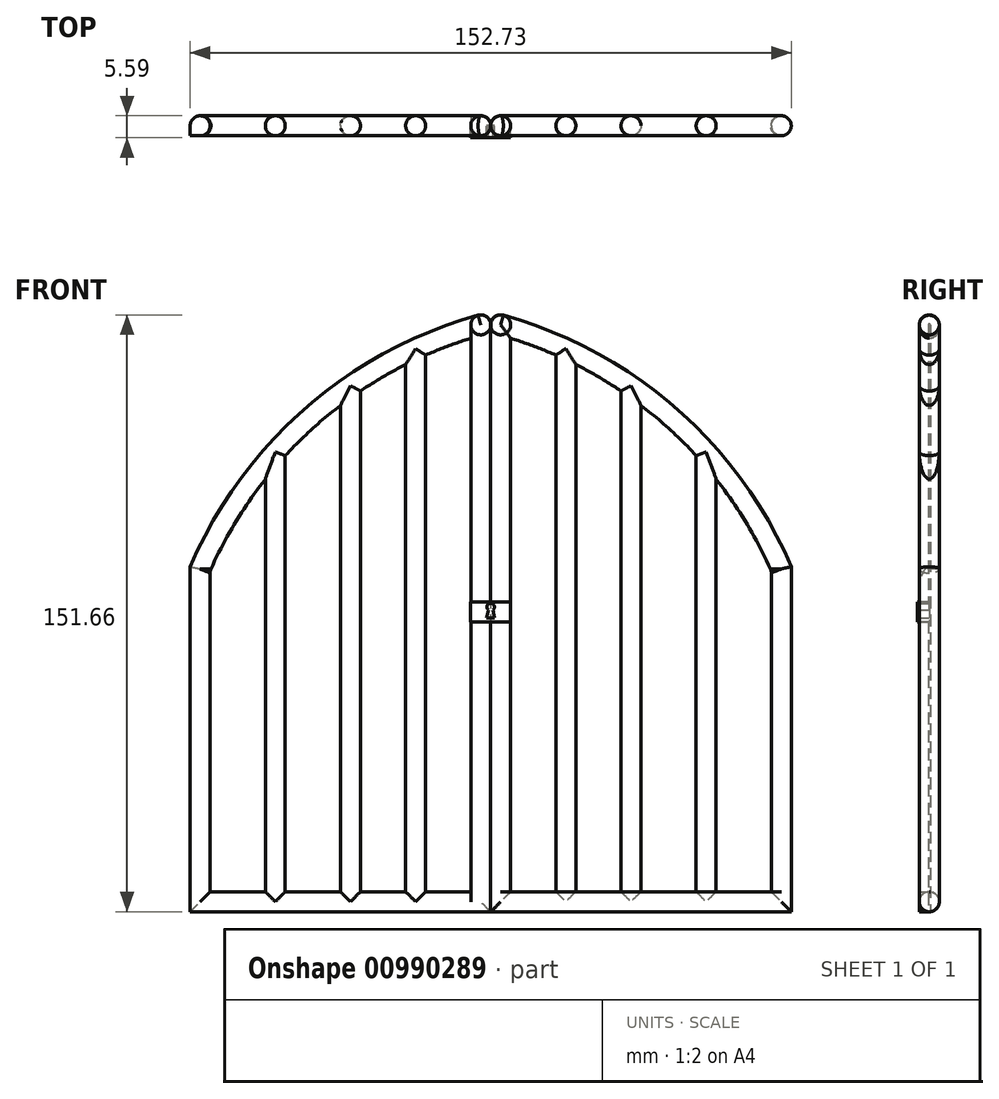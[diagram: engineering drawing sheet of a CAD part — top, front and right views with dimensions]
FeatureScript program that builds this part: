
annotation { "Feature Type Name" : "Feature", "Feature Type Description" : "" }
export const myFeature = defineFeature(function(context is Context, id is Id, definition is map)
    precondition{}
    {
        {
            var Q0;
            Q0=qCreatedBy(makeId("Front.planeOp"),FACE);
            var sketch = newSketch(context, id + "F0", { "sketchPlane" : qUnion([Q0])});
            skLineSegment(sketch, "E0", {"start": v(0, -76.2) * mm, "end": v(-76.38, -76.2) * mm});
            skLineSegment(sketch, "E1", {"start": v(-76.38, -76.2) * mm, "end": v(-76.38, 11.44) * mm});
            skArc(sketch, "E2", {"start": v(0, 76.2) * mm, "mid": v(-45.83, 52.84) * mm, "end": v(-76.38, 11.44) * mm});
            skLineSegment(sketch, "E3.MirrorCS", {"start": v(76.38, -76.2) * mm, "end": v(76.38, 11.44) * mm});
            skLineSegment(sketch, "E4.MirrorCS", {"start": v(0, -76.2) * mm, "end": v(76.38, -76.2) * mm});
            skArc(sketch, "E5.MirrorCS", {"start": v(0, 76.2) * mm, "mid": v(45.83, 52.84) * mm, "end": v(76.38, 11.44) * mm});
            skArc(sketch, "E6.0", {"start": v(5.08, 69.52) * mm, "mid": v(10.88, 67.54) * mm, "end": v(16.55, 65.23) * mm});
            skLineSegment(sketch, "E6.1", {"start": v(-71.3, -71.12) * mm, "end": v(-71.3, 10.4) * mm});
            skLineSegment(sketch, "E6.2", {"start": v(-5.08, -71.12) * mm, "end": v(-16.55, -71.12) * mm});
            skArc(sketch, "E6.3", {"start": v(-5.08, 69.52) * mm, "mid": v(-10.88, 67.54) * mm, "end": v(-16.55, 65.23) * mm});
            skLineSegment(sketch, "E6.4", {"start": v(5.08, -71.12) * mm, "end": v(16.55, -71.12) * mm});
            skLineSegment(sketch, "E6.5", {"start": v(71.3, -71.12) * mm, "end": v(71.3, 10.4) * mm});
            skLineSegment(sketch, "E7", {"start": v(-5.08, 69.52) * mm, "end": v(-5.08, -71.12) * mm});
            skLineSegment(sketch, "E8", {"start": v(5.08, 69.52) * mm, "end": v(5.08, -71.12) * mm});
            skLineSegment(sketch, "E9", {"start": v(33.1, -71.12) * mm, "end": v(33.1, 56.1) * mm});
            skLineSegment(sketch, "E10", {"start": v(38.19, -71.12) * mm, "end": v(38.19, 52.47) * mm});
            skLineSegment(sketch, "E11", {"start": v(16.55, -71.12) * mm, "end": v(16.55, 65.23) * mm});
            skLineSegment(sketch, "E12", {"start": v(21.63, -71.12) * mm, "end": v(21.63, 62.83) * mm});
            skLineSegment(sketch, "E13", {"start": v(38.19, -71.12) * mm, "end": v(52.2, -71.12) * mm});
            skLineSegment(sketch, "E14", {"start": v(52.2, -71.12) * mm, "end": v(52.2, 39.68) * mm});
            skLineSegment(sketch, "E15", {"start": v(57.28, -71.12) * mm, "end": v(57.28, 33.71) * mm});
            skLineSegment(sketch, "E16.MirrorCS", {"start": v(-16.55, -71.12) * mm, "end": v(-16.55, 65.23) * mm});
            skLineSegment(sketch, "E17.MirrorCS", {"start": v(-21.63, -71.12) * mm, "end": v(-21.63, 62.83) * mm});
            skLineSegment(sketch, "E18.MirrorCS", {"start": v(-33.1, -71.12) * mm, "end": v(-33.1, 56.1) * mm});
            skLineSegment(sketch, "E19.MirrorCS", {"start": v(-38.19, -71.12) * mm, "end": v(-38.19, 52.47) * mm});
            skLineSegment(sketch, "E20.MirrorCS", {"start": v(-52.2, -71.12) * mm, "end": v(-52.2, 39.68) * mm});
            skLineSegment(sketch, "E21.MirrorCS", {"start": v(-57.28, -71.12) * mm, "end": v(-57.28, 33.71) * mm});
            skPoint(sketch, "E22.end.orphan", {"position": v(-5.08, 70.96) * mm});
            skPoint(sketch, "E22.start.orphan", {"position": v(5.08, 70.96) * mm});
            skArc(sketch, "E23.trimOffspring", {"start": v(21.63, 62.83) * mm, "mid": v(27.48, 59.65) * mm, "end": v(33.1, 56.1) * mm});
            skArc(sketch, "E24.trimOffspring", {"start": v(38.19, 52.47) * mm, "mid": v(45.48, 46.38) * mm, "end": v(52.2, 39.68) * mm});
            skArc(sketch, "E25.trimOffspring", {"start": v(57.28, 33.71) * mm, "mid": v(65.03, 22.5) * mm, "end": v(71.3, 10.4) * mm});
            skLineSegment(sketch, "E26.trimOffspring", {"start": v(57.28, -71.12) * mm, "end": v(71.3, -71.12) * mm});
            skPoint(sketch, "E27.start.orphan", {"position": v(54.74, -71.12) * mm});
            skPoint(sketch, "E28.start.orphan", {"position": v(35.65, -71.12) * mm});
            skLineSegment(sketch, "E29.trimOffspring", {"start": v(21.63, -71.12) * mm, "end": v(33.1, -71.12) * mm});
            skPoint(sketch, "E30.start.orphan", {"position": v(19.1, -71.12) * mm});
            skPoint(sketch, "E31.orphan", {"position": v(0, -71.12) * mm});
            skLineSegment(sketch, "E32.trimOffspring", {"start": v(-21.63, -71.12) * mm, "end": v(-33.1, -71.12) * mm});
            skLineSegment(sketch, "E33.trimOffspring", {"start": v(-38.19, -71.12) * mm, "end": v(-52.2, -71.12) * mm});
            skLineSegment(sketch, "E34.trimOffspring", {"start": v(-57.28, -71.12) * mm, "end": v(-71.3, -71.12) * mm});
            skArc(sketch, "E35.trimOffspring", {"start": v(-57.28, 33.71) * mm, "mid": v(-65.03, 22.5) * mm, "end": v(-71.3, 10.4) * mm});
            skArc(sketch, "E36.trimOffspring", {"start": v(-21.63, 62.83) * mm, "mid": v(-27.48, 59.65) * mm, "end": v(-33.1, 56.1) * mm});
            skArc(sketch, "E37.trimOffspring", {"start": v(-38.19, 52.47) * mm, "mid": v(-45.48, 46.38) * mm, "end": v(-52.2, 39.68) * mm});
            skLineSegment(sketch, "E38", {"start": v(0, -76.2) * mm, "end": v(0, 76.2) * mm});
            skSolve(sketch);
        }
        {
            var Q0;
            Q0=makeQuery(id+"F0.imprint","IMPRINT",FACE,{"disambiguationData":[TD([[makeQuery(id+"F0.imprint","IMPRINT",EDGE,{"derivedFrom":sQuery(id+"F0.wireOp",EDGE,"E3.MirrorCS")}),1.0]])]});
            extrude(context, id + "F1", {"entities" : qUnion([Q0]), "depth" : 5.08 * mm, "offsetDistance" : 25.4 * mm});
        }
        {
            var Q0;
            Q0=makeQuery(id+"F0.imprint","IMPRINT",FACE,{"disambiguationData":[TD([[makeQuery(id+"F0.imprint","IMPRINT",EDGE,{"derivedFrom":sQuery(id+"F0.wireOp",EDGE,"E0")}),-1.0]])]});
            extrude(context, id + "F2", {"entities" : qUnion([Q0]), "depth" : 5.08 * mm, "offsetDistance" : 25.4 * mm});
        }
        {
            var Q0;
            Q0=makeQuery(id+"F1.opExtrude","CAP_EDGE",EDGE,{"disambiguationData":[OSD([sQuery(id+"F0.wireOp",EDGE,"E7")])],"isStart":false});
            var Q1;
            Q1=makeQuery(id+"F1.opExtrude","CAP_EDGE",EDGE,{"disambiguationData":[OSD([sQuery(id+"F0.wireOp",EDGE,"E8")])],"isStart":false});
            var Q2;
            Q2=makeQuery(id+"F1.opExtrude","CAP_EDGE",EDGE,{"disambiguationData":[OSD([sQuery(id+"F0.wireOp",EDGE,"E11")])],"isStart":false});
            var Q3;
            Q3=makeQuery(id+"F1.opExtrude","CAP_EDGE",EDGE,{"disambiguationData":[OSD([sQuery(id+"F0.wireOp",EDGE,"E12")])],"isStart":false});
            var Q4;
            Q4=makeQuery(id+"F1.opExtrude","CAP_EDGE",EDGE,{"disambiguationData":[OSD([sQuery(id+"F0.wireOp",EDGE,"E9")])],"isStart":false});
            var Q5;
            Q5=makeQuery(id+"F1.opExtrude","CAP_EDGE",EDGE,{"disambiguationData":[OSD([sQuery(id+"F0.wireOp",EDGE,"E10")])],"isStart":false});
            var Q6;
            Q6=makeQuery(id+"F1.opExtrude","CAP_EDGE",EDGE,{"disambiguationData":[OSD([sQuery(id+"F0.wireOp",EDGE,"E14")])],"isStart":false});
            var Q7;
            Q7=makeQuery(id+"F1.opExtrude","CAP_EDGE",EDGE,{"disambiguationData":[OSD([sQuery(id+"F0.wireOp",EDGE,"E15")])],"isStart":false});
            var Q8;
            Q8=makeQuery(id+"F1.opExtrude","CAP_EDGE",EDGE,{"disambiguationData":[OSD([sQuery(id+"F0.wireOp",EDGE,"E16.MirrorCS")])],"isStart":false});
            var Q9;
            Q9=makeQuery(id+"F1.opExtrude","CAP_EDGE",EDGE,{"disambiguationData":[OSD([sQuery(id+"F0.wireOp",EDGE,"E17.MirrorCS")])],"isStart":false});
            var Q10;
            Q10=makeQuery(id+"F1.opExtrude","CAP_EDGE",EDGE,{"disambiguationData":[OSD([sQuery(id+"F0.wireOp",EDGE,"E18.MirrorCS")])],"isStart":false});
            var Q11;
            Q11=makeQuery(id+"F1.opExtrude","CAP_EDGE",EDGE,{"disambiguationData":[OSD([sQuery(id+"F0.wireOp",EDGE,"E19.MirrorCS")])],"isStart":false});
            var Q12;
            Q12=makeQuery(id+"F1.opExtrude","CAP_EDGE",EDGE,{"disambiguationData":[OSD([sQuery(id+"F0.wireOp",EDGE,"E20.MirrorCS")])],"isStart":false});
            var Q13;
            Q13=makeQuery(id+"F1.opExtrude","CAP_EDGE",EDGE,{"disambiguationData":[OSD([sQuery(id+"F0.wireOp",EDGE,"E21.MirrorCS")])],"isStart":false});
            var Q14;
            Q14=makeQuery(id+"F1.opExtrude","CAP_EDGE",EDGE,{"disambiguationData":[OSD([sQuery(id+"F0.wireOp",EDGE,"E6.1")])],"isStart":false});
            var Q15;
            Q15=makeQuery(id+"F1.opExtrude","CAP_EDGE",EDGE,{"disambiguationData":[OSD([sQuery(id+"F0.wireOp",EDGE,"E1")])],"isStart":false});
            var Q16;
            Q16=makeQuery(id+"F1.opExtrude","CAP_EDGE",EDGE,{"disambiguationData":[OSD([sQuery(id+"F0.wireOp",EDGE,"E2")])],"isStart":false});
            var Q17;
            Q17=makeQuery(id+"F1.opExtrude","CAP_EDGE",EDGE,{"disambiguationData":[OSD([sQuery(id+"F0.wireOp",EDGE,"E35.trimOffspring")])],"isStart":false});
            var Q18;
            Q18=makeQuery(id+"F1.opExtrude","CAP_EDGE",EDGE,{"disambiguationData":[OSD([sQuery(id+"F0.wireOp",EDGE,"E37.trimOffspring")])],"isStart":false});
            var Q19;
            Q19=makeQuery(id+"F1.opExtrude","CAP_EDGE",EDGE,{"disambiguationData":[OSD([sQuery(id+"F0.wireOp",EDGE,"E36.trimOffspring")])],"isStart":false});
            var Q20;
            Q20=makeQuery(id+"F1.opExtrude","CAP_EDGE",EDGE,{"disambiguationData":[OSD([sQuery(id+"F0.wireOp",EDGE,"E6.3")])],"isStart":false});
            var Q21;
            Q21=makeQuery(id+"F1.opExtrude","CAP_EDGE",EDGE,{"disambiguationData":[OSD([sQuery(id+"F0.wireOp",EDGE,"E6.0")])],"isStart":false});
            var Q22;
            Q22=makeQuery(id+"F1.opExtrude","CAP_EDGE",EDGE,{"disambiguationData":[OSD([sQuery(id+"F0.wireOp",EDGE,"E24.trimOffspring")])],"isStart":false});
            var Q23;
            Q23=makeQuery(id+"F1.opExtrude","CAP_EDGE",EDGE,{"disambiguationData":[OSD([sQuery(id+"F0.wireOp",EDGE,"E23.trimOffspring")])],"isStart":false});
            var Q24;
            Q24=makeQuery(id+"F1.opExtrude","CAP_EDGE",EDGE,{"disambiguationData":[OSD([sQuery(id+"F0.wireOp",EDGE,"E25.trimOffspring")])],"isStart":false});
            var Q25;
            Q25=makeQuery(id+"F1.opExtrude","CAP_EDGE",EDGE,{"disambiguationData":[OSD([sQuery(id+"F0.wireOp",EDGE,"E5.MirrorCS")])],"isStart":false});
            var Q26;
            Q26=makeQuery(id+"F1.opExtrude","CAP_EDGE",EDGE,{"disambiguationData":[OSD([sQuery(id+"F0.wireOp",EDGE,"E3.MirrorCS")])],"isStart":false});
            var Q27;
            Q27=makeQuery(id+"F1.opExtrude","CAP_EDGE",EDGE,{"disambiguationData":[OSD([sQuery(id+"F0.wireOp",EDGE,"E6.5")])],"isStart":false});
            var Q28;
            Q28=makeQuery(id+"F1.opExtrude","CAP_EDGE",EDGE,{"disambiguationData":[OSD([sQuery(id+"F0.wireOp",EDGE,"E0"),sQuery(id+"F0.wireOp",EDGE,"E4.MirrorCS")])],"isStart":false});
            var Q29;
            Q29=makeQuery(id+"F1.opExtrude","CAP_EDGE",EDGE,{"disambiguationData":[OSD([sQuery(id+"F0.wireOp",EDGE,"E38")])],"isStart":false});
            var Q30;
            Q30=makeQuery(id+"F2.opExtrude","CAP_EDGE",EDGE,{"disambiguationData":[OSD([sQuery(id+"F0.wireOp",EDGE,"E7")])],"isStart":false});
            var Q31;
            Q31=makeQuery(id+"F2.opExtrude","CAP_EDGE",EDGE,{"disambiguationData":[OSD([sQuery(id+"F0.wireOp",EDGE,"E6.3")])],"isStart":false});
            var Q32;
            Q32=makeQuery(id+"F2.opExtrude","CAP_EDGE",EDGE,{"disambiguationData":[OSD([sQuery(id+"F0.wireOp",EDGE,"E16.MirrorCS")])],"isStart":false});
            var Q33;
            Q33=makeQuery(id+"F2.opExtrude","CAP_EDGE",EDGE,{"disambiguationData":[OSD([sQuery(id+"F0.wireOp",EDGE,"E6.2")])],"isStart":false});
            var Q34;
            Q34=makeQuery(id+"F2.opExtrude","CAP_EDGE",EDGE,{"disambiguationData":[OSD([sQuery(id+"F0.wireOp",EDGE,"E32.trimOffspring")])],"isStart":false});
            var Q35;
            Q35=makeQuery(id+"F2.opExtrude","CAP_EDGE",EDGE,{"disambiguationData":[OSD([sQuery(id+"F0.wireOp",EDGE,"E17.MirrorCS")])],"isStart":false});
            var Q36;
            Q36=makeQuery(id+"F2.opExtrude","CAP_EDGE",EDGE,{"disambiguationData":[OSD([sQuery(id+"F0.wireOp",EDGE,"E18.MirrorCS")])],"isStart":false});
            var Q37;
            Q37=makeQuery(id+"F2.opExtrude","CAP_EDGE",EDGE,{"disambiguationData":[OSD([sQuery(id+"F0.wireOp",EDGE,"E36.trimOffspring")])],"isStart":false});
            var Q38;
            Q38=makeQuery(id+"F2.opExtrude","CAP_EDGE",EDGE,{"disambiguationData":[OSD([sQuery(id+"F0.wireOp",EDGE,"E19.MirrorCS")])],"isStart":false});
            var Q39;
            Q39=makeQuery(id+"F2.opExtrude","CAP_EDGE",EDGE,{"disambiguationData":[OSD([sQuery(id+"F0.wireOp",EDGE,"E37.trimOffspring")])],"isStart":false});
            var Q40;
            Q40=makeQuery(id+"F2.opExtrude","CAP_EDGE",EDGE,{"disambiguationData":[OSD([sQuery(id+"F0.wireOp",EDGE,"E33.trimOffspring")])],"isStart":false});
            var Q41;
            Q41=makeQuery(id+"F2.opExtrude","CAP_EDGE",EDGE,{"disambiguationData":[OSD([sQuery(id+"F0.wireOp",EDGE,"E20.MirrorCS")])],"isStart":false});
            var Q42;
            Q42=makeQuery(id+"F2.opExtrude","CAP_EDGE",EDGE,{"disambiguationData":[OSD([sQuery(id+"F0.wireOp",EDGE,"E21.MirrorCS")])],"isStart":false});
            var Q43;
            Q43=makeQuery(id+"F2.opExtrude","CAP_EDGE",EDGE,{"disambiguationData":[OSD([sQuery(id+"F0.wireOp",EDGE,"E34.trimOffspring")])],"isStart":false});
            var Q44;
            Q44=makeQuery(id+"F2.opExtrude","CAP_EDGE",EDGE,{"disambiguationData":[OSD([sQuery(id+"F0.wireOp",EDGE,"E6.1")])],"isStart":false});
            var Q45;
            Q45=makeQuery(id+"F2.opExtrude","CAP_EDGE",EDGE,{"disambiguationData":[OSD([sQuery(id+"F0.wireOp",EDGE,"E35.trimOffspring")])],"isStart":false});
            var Q46;
            Q46=makeQuery(id+"F2.opExtrude","CAP_EDGE",EDGE,{"disambiguationData":[OSD([sQuery(id+"F0.wireOp",EDGE,"E2")])],"isStart":false});
            var Q47;
            Q47=makeQuery(id+"F2.opExtrude","CAP_EDGE",EDGE,{"disambiguationData":[OSD([sQuery(id+"F0.wireOp",EDGE,"E38")])],"isStart":false});
            var Q48;
            Q48=qNothing();
            fillet(context, id + "F3", {"entities" : qUnion([Q0, Q1, Q2, Q3, Q4, Q5, Q6, Q7, Q8, Q9, Q10, Q11, Q12, Q13, Q14, Q15, Q16, Q17, Q18, Q19, Q20, Q21, Q22, Q23, Q24, Q25, Q26, Q27, Q28, Q29, Q30, Q31, Q32, Q33, Q34, Q35, Q36, Q37, Q38, Q39, Q40, Q41, Q42, Q43, Q44, Q45, Q46, Q47, Q48]), "radius" : 2.54 * mm, "tangentPropagation" : true, "allowEdgeOverflow" : false});
        }
        {
            var Q0;
            Q0=makeQuery(id+"F1.opExtrude","CAP_EDGE",EDGE,{"disambiguationData":[OSD([sQuery(id+"F0.wireOp",EDGE,"E7")])],"isStart":true});
            var Q1;
            Q1=makeQuery(id+"F1.opExtrude","CAP_EDGE",EDGE,{"disambiguationData":[OSD([sQuery(id+"F0.wireOp",EDGE,"E8")])],"isStart":true});
            var Q2;
            Q2=makeQuery(id+"F1.opExtrude","CAP_EDGE",EDGE,{"disambiguationData":[OSD([sQuery(id+"F0.wireOp",EDGE,"E11")])],"isStart":true});
            var Q3;
            Q3=makeQuery(id+"F1.opExtrude","CAP_EDGE",EDGE,{"disambiguationData":[OSD([sQuery(id+"F0.wireOp",EDGE,"E12")])],"isStart":true});
            var Q4;
            Q4=makeQuery(id+"F1.opExtrude","CAP_EDGE",EDGE,{"disambiguationData":[OSD([sQuery(id+"F0.wireOp",EDGE,"E9")])],"isStart":true});
            var Q5;
            Q5=makeQuery(id+"F1.opExtrude","CAP_EDGE",EDGE,{"disambiguationData":[OSD([sQuery(id+"F0.wireOp",EDGE,"E10")])],"isStart":true});
            var Q6;
            Q6=makeQuery(id+"F1.opExtrude","CAP_EDGE",EDGE,{"disambiguationData":[OSD([sQuery(id+"F0.wireOp",EDGE,"E14")])],"isStart":true});
            var Q7;
            Q7=makeQuery(id+"F1.opExtrude","CAP_EDGE",EDGE,{"disambiguationData":[OSD([sQuery(id+"F0.wireOp",EDGE,"E15")])],"isStart":true});
            var Q8;
            Q8=makeQuery(id+"F1.opExtrude","CAP_EDGE",EDGE,{"disambiguationData":[OSD([sQuery(id+"F0.wireOp",EDGE,"E6.5")])],"isStart":true});
            var Q9;
            Q9=makeQuery(id+"F1.opExtrude","CAP_EDGE",EDGE,{"disambiguationData":[OSD([sQuery(id+"F0.wireOp",EDGE,"E3.MirrorCS")])],"isStart":true});
            var Q10;
            Q10=makeQuery(id+"F1.opExtrude","CAP_EDGE",EDGE,{"disambiguationData":[OSD([sQuery(id+"F0.wireOp",EDGE,"E16.MirrorCS")])],"isStart":true});
            var Q11;
            Q11=makeQuery(id+"F1.opExtrude","CAP_EDGE",EDGE,{"disambiguationData":[OSD([sQuery(id+"F0.wireOp",EDGE,"E17.MirrorCS")])],"isStart":true});
            var Q12;
            Q12=makeQuery(id+"F1.opExtrude","CAP_EDGE",EDGE,{"disambiguationData":[OSD([sQuery(id+"F0.wireOp",EDGE,"E18.MirrorCS")])],"isStart":true});
            var Q13;
            Q13=makeQuery(id+"F1.opExtrude","CAP_EDGE",EDGE,{"disambiguationData":[OSD([sQuery(id+"F0.wireOp",EDGE,"E19.MirrorCS")])],"isStart":true});
            var Q14;
            Q14=makeQuery(id+"F1.opExtrude","CAP_EDGE",EDGE,{"disambiguationData":[OSD([sQuery(id+"F0.wireOp",EDGE,"E21.MirrorCS")])],"isStart":true});
            var Q15;
            Q15=makeQuery(id+"F1.opExtrude","CAP_EDGE",EDGE,{"disambiguationData":[OSD([sQuery(id+"F0.wireOp",EDGE,"E20.MirrorCS")])],"isStart":true});
            var Q16;
            Q16=makeQuery(id+"F1.opExtrude","CAP_EDGE",EDGE,{"disambiguationData":[OSD([sQuery(id+"F0.wireOp",EDGE,"E6.1")])],"isStart":true});
            var Q17;
            Q17=makeQuery(id+"F1.opExtrude","CAP_EDGE",EDGE,{"disambiguationData":[OSD([sQuery(id+"F0.wireOp",EDGE,"E1")])],"isStart":true});
            var Q18;
            Q18=makeQuery(id+"F1.opExtrude","CAP_EDGE",EDGE,{"disambiguationData":[OSD([sQuery(id+"F0.wireOp",EDGE,"E0"),sQuery(id+"F0.wireOp",EDGE,"E4.MirrorCS")])],"isStart":true});
            var Q19;
            Q19=makeQuery(id+"F2.opExtrude","CAP_EDGE",EDGE,{"disambiguationData":[OSD([sQuery(id+"F0.wireOp",EDGE,"E7")])],"isStart":true});
            var Q20;
            Q20=makeQuery(id+"F2.opExtrude","CAP_EDGE",EDGE,{"disambiguationData":[OSD([sQuery(id+"F0.wireOp",EDGE,"E6.3")])],"isStart":true});
            var Q21;
            Q21=makeQuery(id+"F2.opExtrude","CAP_EDGE",EDGE,{"disambiguationData":[OSD([sQuery(id+"F0.wireOp",EDGE,"E16.MirrorCS")])],"isStart":true});
            var Q22;
            Q22=makeQuery(id+"F2.opExtrude","CAP_EDGE",EDGE,{"disambiguationData":[OSD([sQuery(id+"F0.wireOp",EDGE,"E6.2")])],"isStart":true});
            var Q23;
            Q23=makeQuery(id+"F2.opExtrude","CAP_EDGE",EDGE,{"disambiguationData":[OSD([sQuery(id+"F0.wireOp",EDGE,"E0")])],"isStart":true});
            var Q24;
            Q24=makeQuery(id+"F2.opExtrude","CAP_EDGE",EDGE,{"disambiguationData":[OSD([sQuery(id+"F0.wireOp",EDGE,"E32.trimOffspring")])],"isStart":true});
            var Q25;
            Q25=makeQuery(id+"F2.opExtrude","CAP_EDGE",EDGE,{"disambiguationData":[OSD([sQuery(id+"F0.wireOp",EDGE,"E17.MirrorCS")])],"isStart":true});
            var Q26;
            Q26=makeQuery(id+"F2.opExtrude","CAP_EDGE",EDGE,{"disambiguationData":[OSD([sQuery(id+"F0.wireOp",EDGE,"E18.MirrorCS")])],"isStart":true});
            var Q27;
            Q27=makeQuery(id+"F2.opExtrude","CAP_EDGE",EDGE,{"disambiguationData":[OSD([sQuery(id+"F0.wireOp",EDGE,"E19.MirrorCS")])],"isStart":true});
            var Q28;
            Q28=makeQuery(id+"F2.opExtrude","CAP_EDGE",EDGE,{"disambiguationData":[OSD([sQuery(id+"F0.wireOp",EDGE,"E33.trimOffspring")])],"isStart":true});
            var Q29;
            Q29=makeQuery(id+"F2.opExtrude","CAP_EDGE",EDGE,{"disambiguationData":[OSD([sQuery(id+"F0.wireOp",EDGE,"E20.MirrorCS")])],"isStart":true});
            var Q30;
            Q30=makeQuery(id+"F2.opExtrude","CAP_EDGE",EDGE,{"disambiguationData":[OSD([sQuery(id+"F0.wireOp",EDGE,"E21.MirrorCS")])],"isStart":true});
            var Q31;
            Q31=makeQuery(id+"F2.opExtrude","CAP_EDGE",EDGE,{"disambiguationData":[OSD([sQuery(id+"F0.wireOp",EDGE,"E34.trimOffspring")])],"isStart":true});
            var Q32;
            Q32=makeQuery(id+"F2.opExtrude","CAP_EDGE",EDGE,{"disambiguationData":[OSD([sQuery(id+"F0.wireOp",EDGE,"E6.1")])],"isStart":true});
            var Q33;
            Q33=makeQuery(id+"F2.opExtrude","CAP_EDGE",EDGE,{"disambiguationData":[OSD([sQuery(id+"F0.wireOp",EDGE,"E35.trimOffspring")])],"isStart":true});
            var Q34;
            Q34=makeQuery(id+"F2.opExtrude","CAP_EDGE",EDGE,{"disambiguationData":[OSD([sQuery(id+"F0.wireOp",EDGE,"E37.trimOffspring")])],"isStart":true});
            var Q35;
            Q35=makeQuery(id+"F2.opExtrude","CAP_EDGE",EDGE,{"disambiguationData":[OSD([sQuery(id+"F0.wireOp",EDGE,"E36.trimOffspring")])],"isStart":true});
            var Q36;
            Q36=makeQuery(id+"F2.opExtrude","CAP_EDGE",EDGE,{"disambiguationData":[OSD([sQuery(id+"F0.wireOp",EDGE,"E2")])],"isStart":true});
            var Q37;
            Q37=makeQuery(id+"F3.opFillet","BLEND_EDGE",EDGE,{"blendedFrom":[makeQuery(id+"F2.opExtrude","CAP_EDGE",EDGE,{"disambiguationData":[OSD([sQuery(id+"F0.wireOp",EDGE,"E2")])],"isStart":false}),makeQuery(id+"F2.opExtrude","CAP_EDGE",EDGE,{"disambiguationData":[OSD([sQuery(id+"F0.wireOp",EDGE,"E38")])],"isStart":false})],"blendedInto":[]});
            var Q38;
            Q38=makeQuery(id+"F2.opExtrude","SWEPT_EDGE",EDGE,{"disambiguationData":[OSD([sQuery(id+"F0.wireOp",EDGE,"E2"),sQuery(id+"F0.wireOp",EDGE,"E5.MirrorCS"),sQuery(id+"F0.wireOp",EDGE,"E38")])]});
            var Q39;
            Q39=makeQuery(id+"F2.opExtrude","CAP_EDGE",EDGE,{"disambiguationData":[OSD([sQuery(id+"F0.wireOp",EDGE,"E38")])],"isStart":true});
            var Q40;
            Q40=makeQuery(id+"F1.opExtrude","SWEPT_EDGE",EDGE,{"disambiguationData":[OSD([sQuery(id+"F0.wireOp",EDGE,"E2"),sQuery(id+"F0.wireOp",EDGE,"E5.MirrorCS"),sQuery(id+"F0.wireOp",EDGE,"E38")])]});
            var Q41;
            Q41=makeQuery(id+"F1.opExtrude","CAP_EDGE",EDGE,{"disambiguationData":[OSD([sQuery(id+"F0.wireOp",EDGE,"E38")])],"isStart":true});
            var Q42;
            Q42=makeQuery(id+"F1.opExtrude","CAP_EDGE",EDGE,{"disambiguationData":[OSD([sQuery(id+"F0.wireOp",EDGE,"E5.MirrorCS")])],"isStart":true});
            var Q43;
            Q43=makeQuery(id+"F1.opExtrude","CAP_EDGE",EDGE,{"disambiguationData":[OSD([sQuery(id+"F0.wireOp",EDGE,"E26.trimOffspring")])],"isStart":true});
            var Q44;
            Q44=makeQuery(id+"F1.opExtrude","CAP_EDGE",EDGE,{"disambiguationData":[OSD([sQuery(id+"F0.wireOp",EDGE,"E13")])],"isStart":true});
            var Q45;
            Q45=makeQuery(id+"F1.opExtrude","CAP_EDGE",EDGE,{"disambiguationData":[OSD([sQuery(id+"F0.wireOp",EDGE,"E29.trimOffspring")])],"isStart":true});
            var Q46;
            Q46=makeQuery(id+"F1.opExtrude","CAP_EDGE",EDGE,{"disambiguationData":[OSD([sQuery(id+"F0.wireOp",EDGE,"E6.4")])],"isStart":true});
            var Q47;
            Q47=makeQuery(id+"F1.opExtrude","CAP_EDGE",EDGE,{"disambiguationData":[OSD([sQuery(id+"F0.wireOp",EDGE,"E25.trimOffspring")])],"isStart":true});
            var Q48;
            Q48=makeQuery(id+"F1.opExtrude","CAP_EDGE",EDGE,{"disambiguationData":[OSD([sQuery(id+"F0.wireOp",EDGE,"E24.trimOffspring")])],"isStart":true});
            var Q49;
            Q49=makeQuery(id+"F1.opExtrude","CAP_EDGE",EDGE,{"disambiguationData":[OSD([sQuery(id+"F0.wireOp",EDGE,"E23.trimOffspring")])],"isStart":true});
            var Q50;
            Q50=makeQuery(id+"F1.opExtrude","CAP_EDGE",EDGE,{"disambiguationData":[OSD([sQuery(id+"F0.wireOp",EDGE,"E6.0")])],"isStart":true});
            var Q51;
            Q51=makeQuery(id+"F2.opExtrude","CAP_EDGE",EDGE,{"disambiguationData":[OSD([sQuery(id+"F0.wireOp",EDGE,"E1")])],"isStart":true});
            fillet(context, id + "F4", {"entities" : qUnion([Q0, Q1, Q2, Q3, Q4, Q5, Q6, Q7, Q8, Q9, Q10, Q11, Q12, Q13, Q14, Q15, Q16, Q17, Q18, Q19, Q20, Q21, Q22, Q23, Q24, Q25, Q26, Q27, Q28, Q29, Q30, Q31, Q32, Q33, Q34, Q35, Q36, Q37, Q38, Q39, Q40, Q41, Q42, Q43, Q44, Q45, Q46, Q47, Q48, Q49, Q50, Q51]), "radius" : 2.54 * mm, "tangentPropagation" : true, "allowEdgeOverflow" : false});
        }
        {
            var Q0;
            Q0=makeQuery(id+"F4.opFillet","BLEND_EDGE",EDGE,{"blendedFrom":[makeQuery(id+"F1.opExtrude","CAP_EDGE",EDGE,{"disambiguationData":[OSD([sQuery(id+"F0.wireOp",EDGE,"E6.5")])],"isStart":true}),makeQuery(id+"F1.opExtrude","CAP_EDGE",EDGE,{"disambiguationData":[OSD([sQuery(id+"F0.wireOp",EDGE,"E25.trimOffspring")])],"isStart":true})],"blendedInto":[]});
            var Q1;
            Q1=makeQuery(id+"F4.opFillet","BLEND_EDGE",EDGE,{"blendedFrom":[makeQuery(id+"F2.opExtrude","CAP_EDGE",EDGE,{"disambiguationData":[OSD([sQuery(id+"F0.wireOp",EDGE,"E6.1")])],"isStart":true}),makeQuery(id+"F2.opExtrude","CAP_EDGE",EDGE,{"disambiguationData":[OSD([sQuery(id+"F0.wireOp",EDGE,"E35.trimOffspring")])],"isStart":true})],"blendedInto":[]});
            fillet(context, id + "F5", {"entities" : qUnion([Q0, Q1]), "radius" : 2.54 * mm, "tangentPropagation" : true, "allowEdgeOverflow" : false});
        }
        {
            var Q0;
            Q0=makeQuery(id+"F2.opExtrude","SWEPT_BODY",BODY,{"disambiguationData":[OSD([sQuery(id+"F0.wireOp",EDGE,"E0"),sQuery(id+"F0.wireOp",EDGE,"E1"),sQuery(id+"F0.wireOp",EDGE,"E2"),sQuery(id+"F0.wireOp",EDGE,"E6.1"),sQuery(id+"F0.wireOp",EDGE,"E6.2"),sQuery(id+"F0.wireOp",EDGE,"E6.3"),sQuery(id+"F0.wireOp",EDGE,"E7"),sQuery(id+"F0.wireOp",EDGE,"E16.MirrorCS"),sQuery(id+"F0.wireOp",EDGE,"E17.MirrorCS"),sQuery(id+"F0.wireOp",EDGE,"E18.MirrorCS"),sQuery(id+"F0.wireOp",EDGE,"E19.MirrorCS"),sQuery(id+"F0.wireOp",EDGE,"E20.MirrorCS"),sQuery(id+"F0.wireOp",EDGE,"E21.MirrorCS"),sQuery(id+"F0.wireOp",EDGE,"E32.trimOffspring"),sQuery(id+"F0.wireOp",EDGE,"E33.trimOffspring"),sQuery(id+"F0.wireOp",EDGE,"E34.trimOffspring"),sQuery(id+"F0.wireOp",EDGE,"E35.trimOffspring"),sQuery(id+"F0.wireOp",EDGE,"E36.trimOffspring"),sQuery(id+"F0.wireOp",EDGE,"E37.trimOffspring"),sQuery(id+"F0.wireOp",EDGE,"E38")])]});
            var Q1;
            Q1=sQuery(id+"F0.wireOp",EDGE,"E0");
            transform(context, id + "F6", {"entities" : qUnion([Q0]), "transformType" : TransformType.TRANSLATION_DISTANCE, "transformDirection" : qUnion([Q1]), "distance" : 0.03 * mm, "oppositeDirection" : true, "makeCopy" : false});
        }
        {
            var Q0;
            Q0=makeQuery(id+"F0.imprint","IMPRINT",FACE,{"disambiguationData":[TD([[makeQuery(id+"F0.imprint","IMPRINT",EDGE,{"derivedFrom":sQuery(id+"F0.wireOp",EDGE,"E6.2")}),-1.0]])]});
            var sketch = newSketch(context, id + "F7", { "sketchPlane" : qUnion([Q0])});
            skLineSegment(sketch, "E39.bottom", {"start": v(-5.08, 2.54) * mm, "end": v(5.08, 2.54) * mm});
            skLineSegment(sketch, "E39.top", {"start": v(-5.08, -2.54) * mm, "end": v(5.08, -2.54) * mm});
            skLineSegment(sketch, "E39.left", {"start": v(-5.08, 2.54) * mm, "end": v(-5.08, -2.54) * mm});
            skLineSegment(sketch, "E39.right", {"start": v(5.08, 2.54) * mm, "end": v(5.08, -2.54) * mm});
            skPoint(sketch, "E39.middle", {"position": v(0, 0) * mm});
            skArc(sketch, "E40", {"start": v(0.6, 0.5) * mm, "mid": v(0, 2.2) * mm, "end": v(-0.6, 0.5) * mm});
            skLineSegment(sketch, "E41", {"start": v(-0.6, 0.5) * mm, "end": v(-1.02, -1.53) * mm});
            skLineSegment(sketch, "E42.MirrorCS", {"start": v(0.6, 0.5) * mm, "end": v(1.02, -1.53) * mm});
            skLineSegment(sketch, "E43", {"start": v(-1.02, -1.53) * mm, "end": v(1.02, -1.53) * mm});
            skSolve(sketch);
        }
        {
            var Q0;
            Q0=makeQuery(id+"F7.imprint","IMPRINT",FACE,{"disambiguationData":[TD([[makeQuery(id+"F7.imprint","IMPRINT",EDGE,{"derivedFrom":sQuery(id+"F7.wireOp",EDGE,"E39.bottom")}),-1.0]])]});
            extrude(context, id + "F8", {"entities" : qUnion([Q0]), "operationType" : NewBodyOperationType.ADD, "depth" : 5.6 * mm, "offsetDistance" : 25.4 * mm, "hasSecondDirection" : true, "secondDirectionOppositeDirection" : false, "secondDirectionDepth" : 2.54 * mm});
        }
        {
            var Q0;
            Q0=makeQuery(id+"F7.imprint","IMPRINT",FACE,{"disambiguationData":[TD([[makeQuery(id+"F7.imprint","IMPRINT",EDGE,{"derivedFrom":sQuery(id+"F7.wireOp",EDGE,"E40")}),1.0]])]});
            extrude(context, id + "F9", {"entities" : qUnion([Q0]), "operationType" : NewBodyOperationType.REMOVE, "depth" : 25.4 * mm, "offsetDistance" : 25.4 * mm, "hasSecondDirection" : true, "secondDirectionOppositeDirection" : false, "secondDirectionDepth" : 2.54 * mm});
        }
    });
